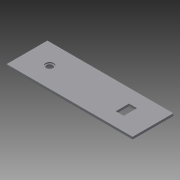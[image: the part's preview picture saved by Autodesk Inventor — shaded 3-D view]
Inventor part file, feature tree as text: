
AUTODESK INVENTOR PART (.ipt)
format: ipt  version: 2015 SP1 (Build 190203100, 203)  size: 94,208 bytes
history: native  units: mm
features: extrude x3, sketch x3, hole x1
ambient origin geometry x8: Origin, YZ Plane, XZ Plane, XY Plane, X Axis, Y Axis, Z Axis, Center Point
bodies: Solid1 (feature_tree)
feature tree (7):
  extrude  "Extrusion1"  Depth=144.0mm
  hole  "Hole1"  [1 undecoded]
  extrude  "Extrusion2"  Depth=80.0mm
  extrude  "Extrusion3"  Depth=4.0mm
  sketch  "Sketch1"  dims[d0=445.0mm d1=144.0mm]
  sketch  "Sketch2"  dims[d2=72.0mm d3=222.5mm]
  sketch  "Sketch3"  dims[d4=8.0mm d5=0.0mm d6=80.0mm d7=72.0mm d8=22.0mm d9=6.0mm d10=4.0mm d11=2.0mm d12=90.0deg d13=8.0mm d14=20.594885mm d15=29.0mm d16=4.0mm d17=0.0mm d18=28.0mm d19=47.0mm d20=80.0mm d21=23.5mm d22=4.0mm d23=0.0mm]
note: 1 required parameter value undecoded (feature->parameter linkage not recoverable at this tier; creation-order binding heuristic only, values carry confidence <= 0.55)
